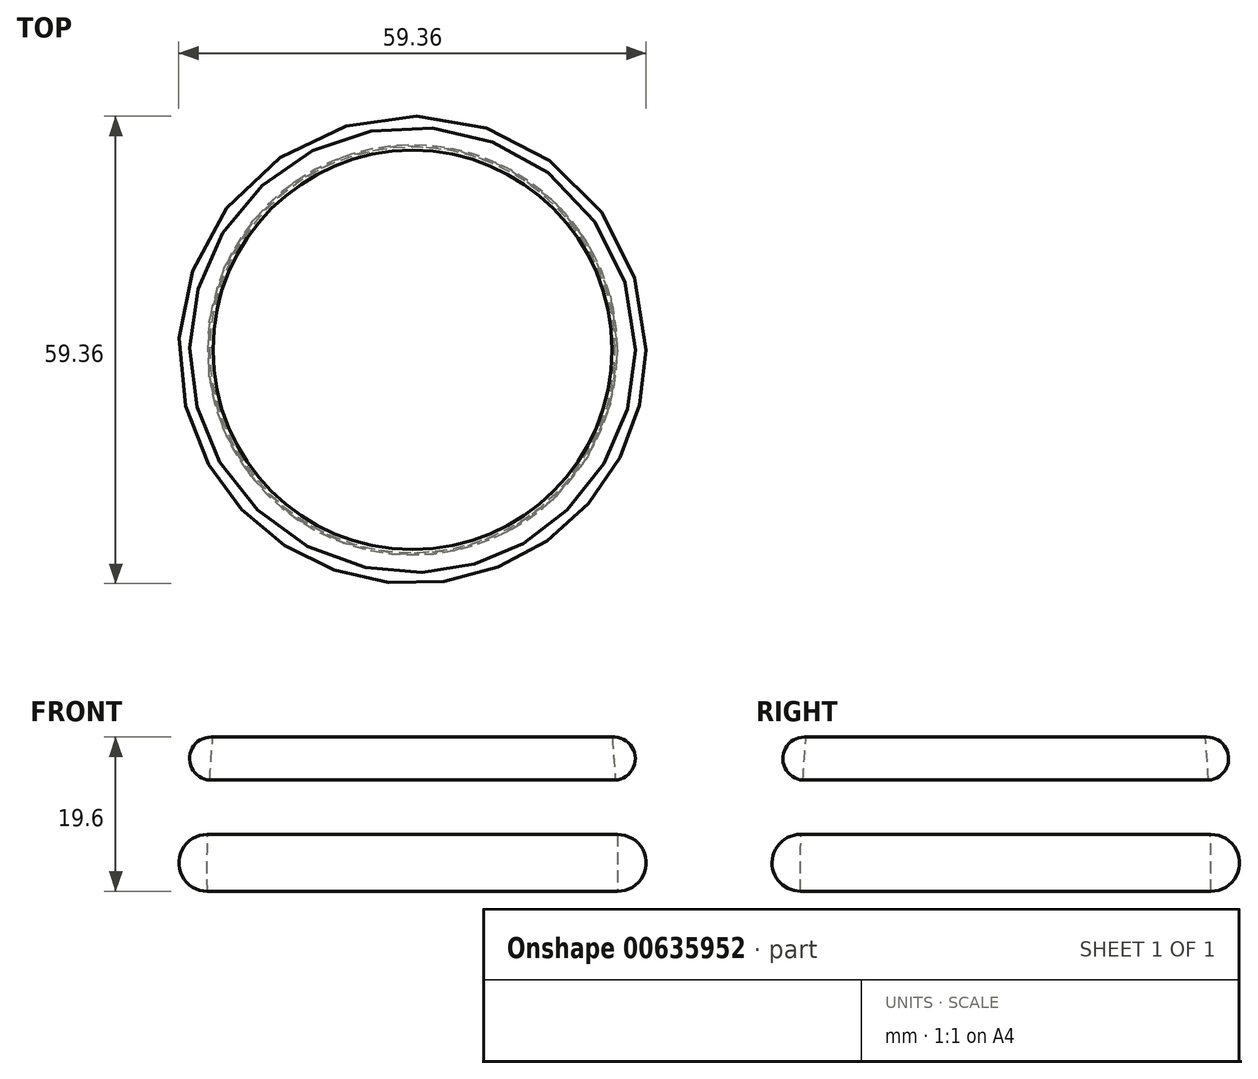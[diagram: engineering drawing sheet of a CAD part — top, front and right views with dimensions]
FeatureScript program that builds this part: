
annotation { "Feature Type Name" : "Feature", "Feature Type Description" : "" }
export const myFeature = defineFeature(function(context is Context, id is Id, definition is map)
    precondition{}
    {
        {
            var Q0;
            Q0=qCreatedBy(makeId("Front.planeOp"),FACE);
            var sketch = newSketch(context, id + "F0", { "sketchPlane" : qUnion([Q0])});
            skFitSpline(sketch, "E0", {"points": [v(-14.7, 53.07) * mm, v(-20.17, 43.7) * mm, v(-23.88, 29.63) * mm, v(-26.03, 5.6) * mm, v(-23.3, -10.82) * mm], "startDerivative": vector(-51.55, -63.01) * mm, "endDerivative": vector(32.4, 0) * mm});
            skLineSegment(sketch, "E1", {"start": v(0, 51.83) * mm, "end": v(0, 49.82) * mm});
            skLineSegment(sketch, "E2", {"start": v(0, 49.82) * mm, "end": v(-13.23, 49.82) * mm});
            skFitSpline(sketch, "E3.0", {"points": [v(-12.24, 51.06) * mm, v(-13.23, 49.85) * mm, v(-14.36, 48.35) * mm, v(-15.36, 46.79) * mm, v(-15.93, 45.75) * mm, v(-16.4, 44.75) * mm, v(-16.74, 43.85) * mm, v(-17.03, 43.06) * mm, v(-17.25, 42.4) * mm, v(-17.48, 41.72) * mm, v(-17.95, 40.28) * mm, v(-18.68, 37.89) * mm, v(-19.64, 34.3) * mm, v(-20.52, 30.41) * mm, v(-21.26, 26.37) * mm, v(-21.84, 22.12) * mm, v(-22.22, 18.37) * mm, v(-22.45, 15.24) * mm, v(-22.6, 12.81) * mm, v(-22.72, 10.3) * mm, v(-22.8, 8.15) * mm, v(-22.84, 6.38) * mm, v(-22.88, 4.58) * mm, v(-22.9, 2.3) * mm, v(-22.89, -0.39) * mm, v(-22.81, -2.5) * mm, v(-22.7, -4.03) * mm, v(-22.6, -5.1) * mm, v(-22.48, -6.06) * mm, v(-22.35, -6.75) * mm, v(-22.25, -7.23) * mm, v(-22.16, -7.54) * mm, v(-22.08, -7.8) * mm, v(-22, -8.02) * mm, v(-21.95, -8.15) * mm, v(-21.92, -8.22) * mm, v(-21.9, -8.25) * mm, v(-21.9, -8.26) * mm, v(-21.9, -8.26) * mm, v(-21.9, -8.27) * mm, v(-21.9, -8.27) * mm, v(-21.9, -8.27) * mm, v(-21.9, -8.27) * mm, v(-21.9, -8.27) * mm, v(-21.89, -8.28) * mm, v(-21.88, -8.28) * mm, v(-21.88, -8.3) * mm, v(-21.86, -8.31) * mm, v(-21.85, -8.34) * mm, v(-21.83, -8.37) * mm, v(-21.8, -8.41) * mm, v(-21.75, -8.49) * mm, v(-21.7, -8.55) * mm, v(-21.68, -8.6) * mm]});
            skLineSegment(sketch, "E4", {"start": v(-26.04, -0.84) * mm, "end": v(-22.86, -0.81) * mm});
            skPoint(sketch, "E5.orphan", {"position": v(-14.7, 49.82) * mm});
            skArc(sketch, "E6", {"start": v(-25.36, 18.75) * mm, "mid": v(-28.3, 16.22) * mm, "end": v(-25.75, 13.3) * mm});
            skArc(sketch, "E7", {"start": v(-26.01, 6.38) * mm, "mid": v(-29.68, 2.78) * mm, "end": v(-26.03, -0.84) * mm});
            skFitSpline(sketch, "E8", {"points": [v(0, 51.83) * mm, v(-7.87, 51.83) * mm, v(-14.7, 53.07) * mm], "startDerivative": vector(-15.57, -0.66) * mm, "endDerivative": vector(-13.81, 3.17) * mm});
            skSolve(sketch);
        }
        {
            var Q0;
            Q0 = qSketchRegion(id + "F0", true);
            var Q1;
            Q1=sQuery(id+"F0.wireOp",EDGE,"E1");
            revolve(context, id + "F1", {"entities" : qUnion([Q0]), "axis" : qUnion([Q1]), "revolveType" : RevolveType.FULL});
        }
    });
